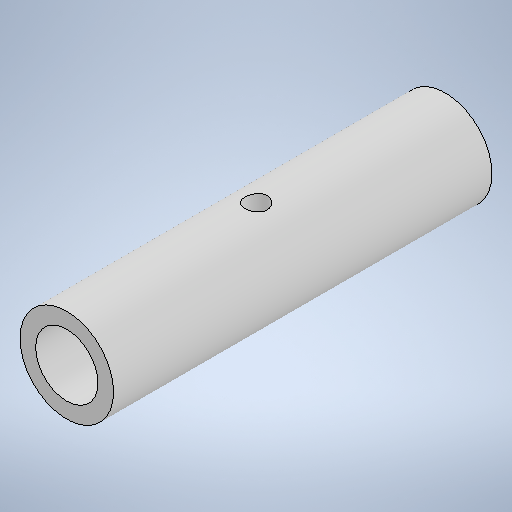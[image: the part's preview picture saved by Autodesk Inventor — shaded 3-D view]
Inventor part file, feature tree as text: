
AUTODESK INVENTOR PART (.ipt)
format: ipt  version: 2025 (Build 290162010, 162A)  size: 240,640 bytes
history: native  units: mm
features: sketch x2, extrude x1, plane x1, hole x1
ambient origin geometry x8: Origin, YZ Plane, XZ Plane, XY Plane, X Axis, Y Axis, Z Axis, Center Point
bodies: Solid1 (feature_tree)
feature tree (5):
  extrude  "Extrusion1"  Depth=14.0mm
  plane  "Work Plane1"
  hole  "Hole1"  [1 undecoded]
  sketch  "Sketch1"  dims[d0=21.0mm d1=14.0mm]
  sketch  "Sketch2"  dims[d2=85.0mm d3=0.0mm d4=-10.75mm d5=42.5mm d6=5.0mm d7=6.0mm d8=4.0mm d9=2.0mm d10=90.0deg d11=8.0mm d12=0.0mm]
note: 1 required parameter value undecoded (feature->parameter linkage not recoverable at this tier; creation-order binding heuristic only, values carry confidence <= 0.55)
